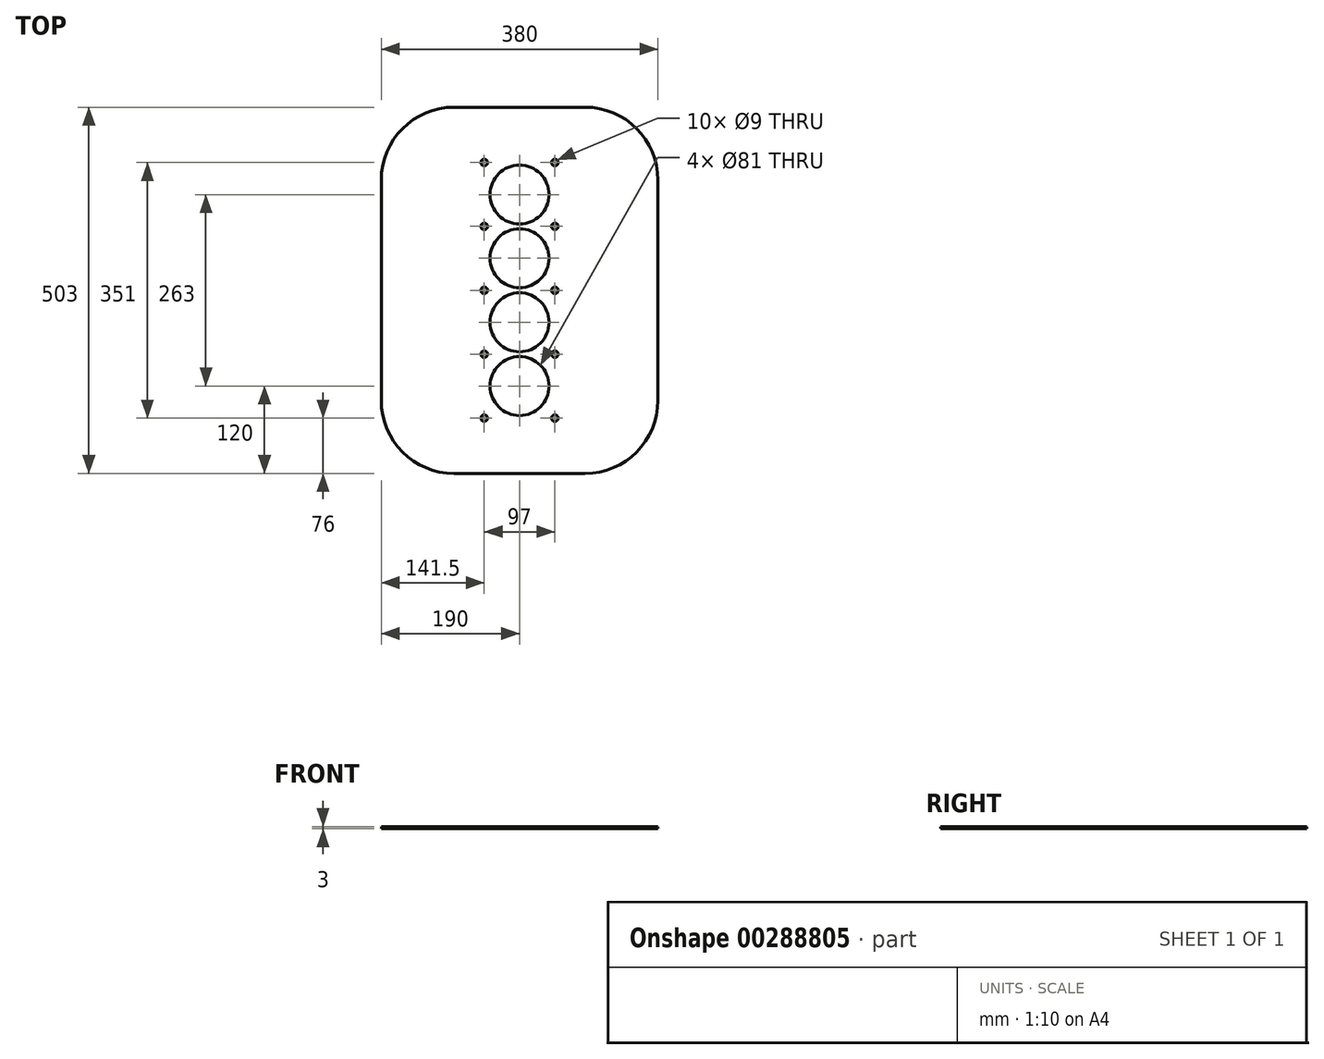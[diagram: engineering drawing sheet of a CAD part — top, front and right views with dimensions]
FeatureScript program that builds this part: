
annotation { "Feature Type Name" : "Feature", "Feature Type Description" : "" }
export const myFeature = defineFeature(function(context is Context, id is Id, definition is map)
    precondition{}
    {
        {
            var Q0;
            Q0=qCreatedBy(makeId("Top.planeOp"),FACE);
            var sketch = newSketch(context, id + "F0", { "sketchPlane" : qUnion([Q0])});
            skLineSegment(sketch, "E0.bottom", {"start": v(-190, 0) * mm, "end": v(190, 0) * mm});
            skLineSegment(sketch, "E0.top", {"start": v(-190, -503) * mm, "end": v(190, -503) * mm});
            skLineSegment(sketch, "E0.left", {"start": v(-190, 0) * mm, "end": v(-190, -503) * mm});
            skLineSegment(sketch, "E0.right", {"start": v(190, 0) * mm, "end": v(190, -503) * mm});
            skLineSegment(sketch, "E1", {"start": v(0, 0) * mm, "end": v(0, -503) * mm, "construction": true});
            skCircle(sketch, "E2", {"center": v(0, -207.5) * mm, "radius": 40.5 * mm});
            skCircle(sketch, "E3", {"center": v(0, -295.5) * mm, "radius": 40.5 * mm});
            skCircle(sketch, "E4", {"center": v(0, -383) * mm, "radius": 40.5 * mm});
            skCircle(sketch, "E5", {"center": v(0, -120) * mm, "radius": 40.5 * mm});
            skLineSegment(sketch, "E6", {"start": v(48.5, -163.75) * mm, "end": v(-48.5, -163.75) * mm, "construction": true});
            skLineSegment(sketch, "E7", {"start": v(-48.5, -251.5) * mm, "end": v(48.5, -251.5) * mm, "construction": true});
            skLineSegment(sketch, "E8", {"start": v(-48.5, -339.25) * mm, "end": v(48.5, -339.25) * mm, "construction": true});
            skLineSegment(sketch, "E9", {"start": v(-48.5, -76) * mm, "end": v(48.5, -76) * mm, "construction": true});
            skLineSegment(sketch, "E10", {"start": v(-48.5, -427) * mm, "end": v(48.5, -427) * mm, "construction": true});
            skSolve(sketch);
        }
        {
            var Q0;
            Q0 = qSketchRegion(id + "F0", true);
            extrude(context, id + "F1", {"entities" : qUnion([Q0]), "depth" : 3 * mm});
        }
        {
            var Q0;
            Q0=makeQuery(id+"F1.opExtrude","SWEPT_EDGE",EDGE,{"disambiguationData":[OSD([sQuery(id+"F0.wireOp",EDGE,"E0.bottom"),sQuery(id+"F0.wireOp",EDGE,"E0.left")])]});
            var Q1;
            Q1=makeQuery(id+"F1.opExtrude","SWEPT_EDGE",EDGE,{"disambiguationData":[OSD([sQuery(id+"F0.wireOp",EDGE,"E0.bottom"),sQuery(id+"F0.wireOp",EDGE,"E0.right")])]});
            var Q2;
            Q2=makeQuery(id+"F1.opExtrude","SWEPT_EDGE",EDGE,{"disambiguationData":[OSD([sQuery(id+"F0.wireOp",EDGE,"E0.top"),sQuery(id+"F0.wireOp",EDGE,"E0.left")])]});
            var Q3;
            Q3=makeQuery(id+"F1.opExtrude","SWEPT_EDGE",EDGE,{"disambiguationData":[OSD([sQuery(id+"F0.wireOp",EDGE,"E0.top"),sQuery(id+"F0.wireOp",EDGE,"E0.right")])]});
            fillet(context, id + "F2", {"entities" : qUnion([Q0, Q1, Q2, Q3]), "radius" : 100 * mm, "tangentPropagation" : true, "allowEdgeOverflow" : false});
        }
        {
            var Q0;
            Q0=sQuery(id+"F0.wireOp",VERTEX,"E9.start");
            var Q1;
            Q1=sQuery(id+"F0.wireOp",VERTEX,"E9.end");
            var Q2;
            Q2=sQuery(id+"F0.wireOp",VERTEX,"E6.end");
            var Q3;
            Q3=sQuery(id+"F0.wireOp",VERTEX,"E6.start");
            var Q4;
            Q4=sQuery(id+"F0.wireOp",VERTEX,"E7.start");
            var Q5;
            Q5=sQuery(id+"F0.wireOp",VERTEX,"E7.end");
            var Q6;
            Q6=sQuery(id+"F0.wireOp",VERTEX,"E8.start");
            var Q7;
            Q7=sQuery(id+"F0.wireOp",VERTEX,"E8.end");
            var Q8;
            Q8=sQuery(id+"F0.wireOp",VERTEX,"E10.start");
            var Q9;
            Q9=sQuery(id+"F0.wireOp",VERTEX,"E10.end");
            var Q10;
            Q10=makeQuery(id+"F1.opExtrude","SWEPT_BODY",BODY,{"disambiguationData":[OSD([sQuery(id+"F0.wireOp",EDGE,"E0.bottom"),sQuery(id+"F0.wireOp",EDGE,"E0.top"),sQuery(id+"F0.wireOp",EDGE,"E0.left"),sQuery(id+"F0.wireOp",EDGE,"E0.right"),sQuery(id+"F0.wireOp",EDGE,"E2"),sQuery(id+"F0.wireOp",EDGE,"E3"),sQuery(id+"F0.wireOp",EDGE,"E4"),sQuery(id+"F0.wireOp",EDGE,"E5")])]});
            hole(context, id + "F3", {"style" : HoleStyle.SIMPLE, "endStyle" : HoleEndStyle.BLIND, "oppositeDirection" : true, "holeDiameter" : 9 * mm, "holeDepth" : 5 * mm, "tappedDepth" : 12 * mm, "tapClearance" : 3, "locations" : qUnion([Q0, Q1, Q2, Q3, Q4, Q5, Q6, Q7, Q8, Q9]), "scope" : qUnion([Q10])});
        }
    });
